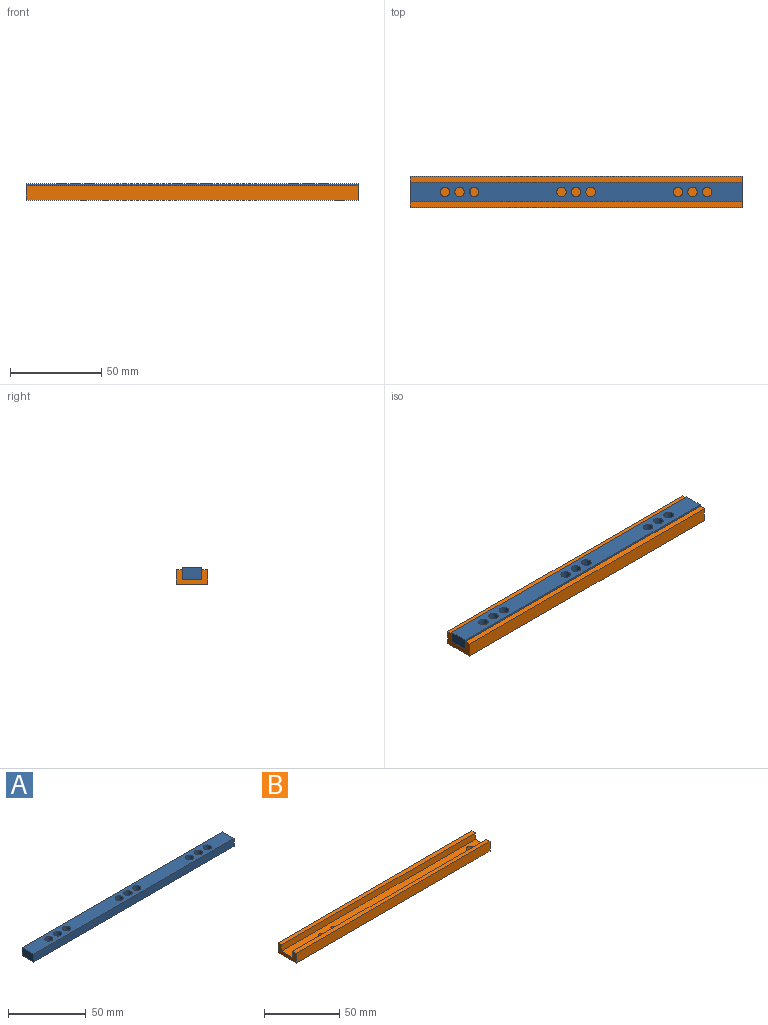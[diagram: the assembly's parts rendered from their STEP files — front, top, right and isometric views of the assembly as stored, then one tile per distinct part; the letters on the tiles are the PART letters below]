
ASSEMBLY  parts=2 mates=1
PART A: 15 faces, bbox 182x10.5x6.2 mm
  f0: plane 182x6.2mm, normal (0,-1,0), area 1128.4mm2, adj f1,f3,f4,f5
  f1: plane 182x10.5mm, normal (0,0,-1), area 1716.2mm2, adj f0,f2,f4,f5,f6,f7,f8,f9
  f2: plane 182x6.2mm, normal (0,1,0), area 1128.4mm2, adj f1,f3,f4,f5
  f3: plane 182x10.5mm, normal (0,0,1), area 1716.2mm2, adj f0,f2,f4,f5,f6,f7,f8,f9
  f4: plane 10.5x6.2mm, normal (1,0,0), area 65.1mm2, adj f0,f1,f2,f3
  f5: plane 10.5x6.2mm, normal (-1,0,0), area 65.1mm2, adj f0,f1,f2,f3
  f6: cylinder r=2.62mm len=6.2mm, axis (0,0,1), area 102.3mm2, adj f1,f3
  f7: cylinder r=2.62mm len=6.2mm, axis (0,0,1), area 102.3mm2, adj f1,f3
  f8: cylinder r=2.62mm len=6.2mm, axis (0,0,1), area 102.3mm2, adj f1,f3
  f9: cylinder r=2.62mm len=6.2mm, axis (0,0,1), area 102.3mm2, adj f1,f3
  f10: cylinder r=2.62mm len=6.2mm, axis (0,0,1), area 102.3mm2, adj f1,f3
  f11: cylinder r=2.62mm len=6.2mm, axis (0,0,1), area 102.3mm2, adj f1,f3
  f12: cylinder r=2.62mm len=6.2mm, axis (0,0,1), area 102.3mm2, adj f1,f3
  f13: cylinder r=2.62mm len=6.2mm, axis (0,0,1), area 102.3mm2, adj f1,f3
  f14: cylinder r=2.62mm len=6.2mm, axis (0,0,1), area 102.3mm2, adj f1,f3
PART B: 13 faces, bbox 182x17x8 mm
  f0: plane 182x3.25mm, normal (0,0,1), area 591.5mm2, adj f1,f7,f8,f9
  f1: plane 182x5.2mm, normal (0,-1,0), area 946.4mm2, adj f0,f2,f8,f9
  f2: plane 182x10.5mm, normal (0,0,1), area 1872.7mm2, adj f1,f3,f8,f9,f10,f11,f12
  f3: plane 182x5.2mm, normal (0,1,0), area 946.4mm2, adj f2,f4,f8,f9
  f4: plane 182x3.25mm, normal (0,0,1), area 591.5mm2, adj f3,f5,f8,f9
  f5: plane 182x8mm, normal (0,-1,0), area 1456mm2, adj f4,f6,f8,f9
  f6: plane 182x17mm, normal (0,0,-1), area 3055.7mm2, adj f5,f7,f8,f9,f10,f11,f12
  f7: plane 182x8mm, normal (0,1,0), area 1456mm2, adj f0,f6,f8,f9
  f8: plane 17x8mm, normal (-1,0,0), area 81.4mm2, adj f0,f1,f2,f3,f4,f5,f6,f7
  f9: plane 17x8mm, normal (1,0,0), area 81.4mm2, adj f0,f1,f2,f3,f4,f5,f6,f7
  f10: cylinder r=2.6mm len=5.2mm, axis (0,0,-1), area 45.7mm2, adj f2,f6
  f11: cylinder r=1.65mm len=3.3mm, axis (0,0,-1), area 29mm2, adj f2,f6
  f12: cylinder r=1.65mm len=3.3mm, axis (0,0,-1), area 29mm2, adj f2,f6
PLACE A t=(-18.08,35.7,-20.66)mm
PLACE B t=(-18.08,35.7,-20.66)mm fixed
MATE planar A.f1 <-> B.f2  axis (0,0,-1) through (163.92,32.47,-8.28)mm
